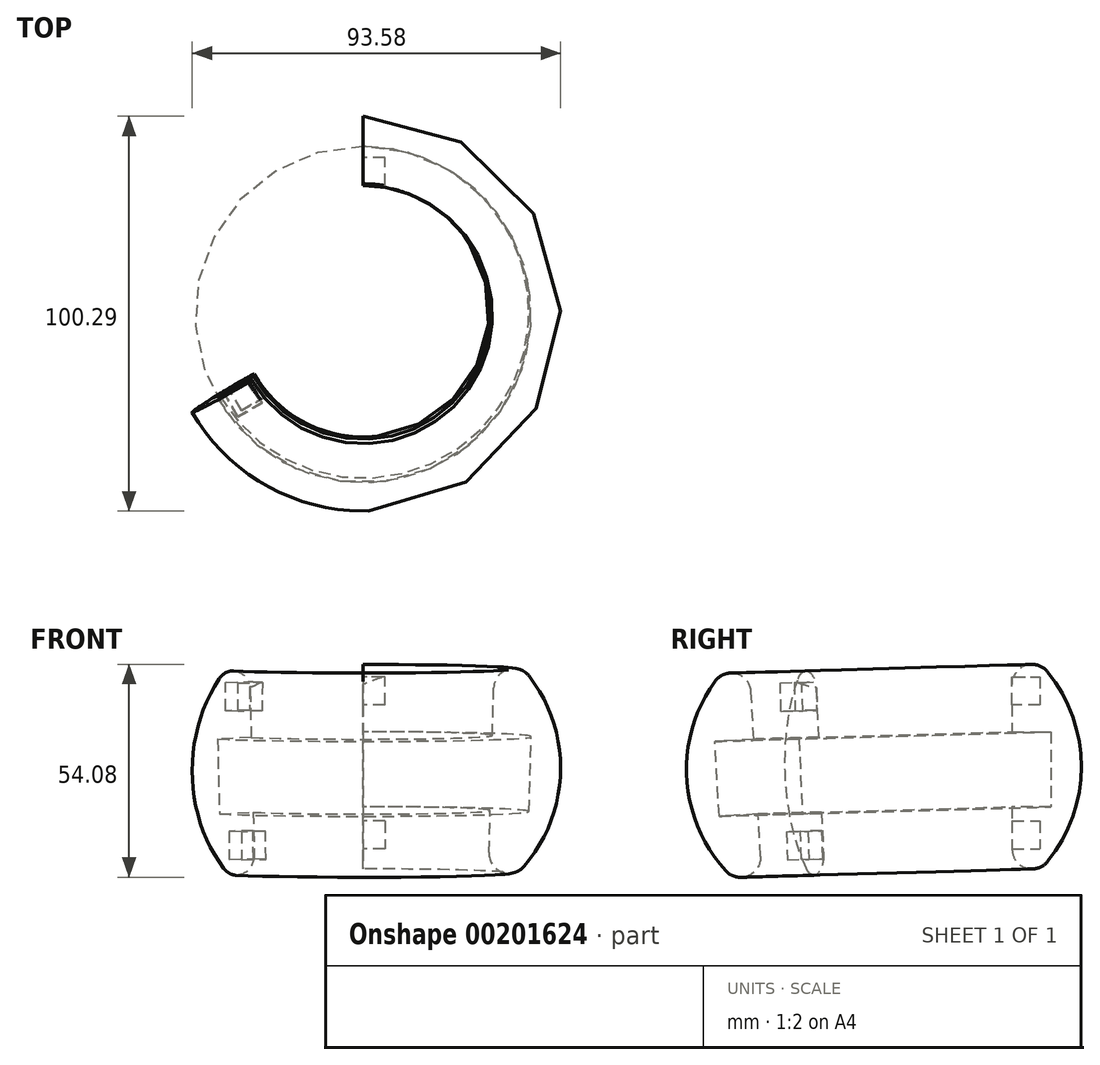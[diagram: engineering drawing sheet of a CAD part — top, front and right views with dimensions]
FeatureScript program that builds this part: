
annotation { "Feature Type Name" : "Feature", "Feature Type Description" : "" }
export const myFeature = defineFeature(function(context is Context, id is Id, definition is map)
    precondition{}
    {
        {
            var Q0;
            Q0=qCreatedBy(makeId("Right.planeOp"),FACE);
            var sketch = newSketch(context, id + "F0", { "sketchPlane" : qUnion([Q0])});
            skArc(sketch, "E0", {"start": v(0, -47.93) * mm, "mid": v(17.57, -15.75) * mm, "end": v(0, 16.43) * mm});
            skLineSegment(sketch, "E1", {"start": v(0, 16.43) * mm, "end": v(0, -6.89) * mm});
            skLineSegment(sketch, "E2", {"start": v(0, -6.89) * mm, "end": v(9.88, -6.89) * mm});
            skLineSegment(sketch, "E3", {"start": v(9.88, -6.89) * mm, "end": v(9.88, -25.94) * mm});
            skLineSegment(sketch, "E4", {"start": v(9.88, -25.94) * mm, "end": v(0, -25.94) * mm});
            skLineSegment(sketch, "E5", {"start": v(0, -25.94) * mm, "end": v(0, -47.93) * mm});
            skSolve(sketch);
        }
        {
            var Q0;
            Q0=qCreatedBy(makeId("Right.planeOp"),FACE);
            var sketch = newSketch(context, id + "F1", { "sketchPlane" : qUnion([Q0])});
            skPoint(sketch, "E6", {"position": v(-32.7, -11.9) * mm});
            skLineSegment(sketch, "E7", {"start": v(-33.24, 7.35) * mm, "end": v(-32.7, -11.9) * mm});
            skSolve(sketch);
        }
        {
            var Q0;
            Q0=qSketchRegion(id+"F0",true);
            var Q1;
            Q1=sQuery(id+"F1.wireOp",EDGE,"E7");
            revolve(context, id + "F2", {"entities" : qUnion([Q0]), "axis" : qUnion([Q1]), "revolveType" : RevolveType.ONE_DIRECTION, "angle" : 240 * degree});
        }
        {
            var Q0;
            Q0=qCreatedBy(makeId("Right.planeOp"),FACE);
            var sketch = newSketch(context, id + "F3", { "sketchPlane" : qUnion([Q0])});
            skLineSegment(sketch, "E8", {"start": v(0, 7.11) * mm, "end": v(7.11, 7.11) * mm});
            skLineSegment(sketch, "E9", {"start": v(7.11, 7.11) * mm, "end": v(7.11, 0) * mm});
            skLineSegment(sketch, "E10", {"start": v(7.11, 0) * mm, "end": v(0, 0) * mm});
            skLineSegment(sketch, "E11", {"start": v(0, 0) * mm, "end": v(0, 7.11) * mm});
            skSolve(sketch);
        }
        {
            var Q0;
            Q0=makeQuery(id+"F3.imprint","IMPRINT",FACE,{"disambiguationData":[TD([[makeQuery(id+"F3.imprint","IMPRINT",EDGE,{"derivedFrom":sQuery(id+"F3.wireOp",EDGE,"E8")}),-1.0]])]});
            extrude(context, id + "F4", {"entities" : qUnion([Q0]), "operationType" : NewBodyOperationType.REMOVE, "depth" : 5.56 * mm});
        }
        {
            var Q0;
            Q0=qCreatedBy(makeId("Right.planeOp"),FACE);
            var sketch = newSketch(context, id + "F5", { "sketchPlane" : qUnion([Q0])});
            skLineSegment(sketch, "E12", {"start": v(0, -29.58) * mm, "end": v(0, -36.7) * mm});
            skLineSegment(sketch, "E13", {"start": v(0, -36.7) * mm, "end": v(7.11, -36.7) * mm});
            skLineSegment(sketch, "E14", {"start": v(0, -29.58) * mm, "end": v(7.11, -29.58) * mm});
            skLineSegment(sketch, "E15", {"start": v(7.11, -29.58) * mm, "end": v(7.11, -36.7) * mm});
            skSolve(sketch);
        }
        {
            var Q0;
            Q0=qSketchRegion(id+"F5",true);
            extrude(context, id + "F6", {"entities" : qUnion([Q0]), "operationType" : NewBodyOperationType.REMOVE, "depth" : 5.56 * mm});
        }
        {
            var Q0;
            Q0=makeQuery(id+"F2.opRevolve","SWEPT_EDGE",EDGE,{"disambiguationData":[OSD([sQuery(id+"F0.wireOp",EDGE,"E0"),sQuery(id+"F0.wireOp",EDGE,"E5")])]});
            fillet(context, id + "F7", {"entities" : qUnion([Q0]), "radius" : 5.08 * mm, "tangentPropagation" : true, "allowEdgeOverflow" : false});
        }
        {
            var Q0;
            Q0=makeQuery(id+"F2.opRevolve","SWEPT_EDGE",EDGE,{"disambiguationData":[OSD([sQuery(id+"F0.wireOp",EDGE,"E0"),sQuery(id+"F0.wireOp",EDGE,"E1")])]});
            fillet(context, id + "F8", {"entities" : qUnion([Q0]), "radius" : 5.08 * mm, "tangentPropagation" : true, "allowEdgeOverflow" : false});
        }
        {
            var Q0;
            Q0=makeQuery(id+"F2.opRevolve","CAP_FACE",FACE,{"disambiguationData":[OSD([sQuery(id+"F0.wireOp",EDGE,"E0"),sQuery(id+"F0.wireOp",EDGE,"E1"),sQuery(id+"F0.wireOp",EDGE,"E2"),sQuery(id+"F0.wireOp",EDGE,"E3"),sQuery(id+"F0.wireOp",EDGE,"E4"),sQuery(id+"F0.wireOp",EDGE,"E5")])],"isStart":false});
            cPlane(context, id + "F9", {"entities" : qUnion([Q0]), "cplaneType" : CPlaneType.OFFSET, "offset" : 0 * mm, "oppositeDirection" : true, "width" : 152.4 * mm, "height" : 152.4 * mm});
        }
        {
            var Q0;
            Q0=qCreatedBy(id+"F9.planeOp",FACE);
            var sketch = newSketch(context, id + "F10", { "sketchPlane" : qUnion([Q0])});
            skLineSegment(sketch, "E16", {"start": v(49.81, 0) * mm, "end": v(56.9, 0) * mm});
            skLineSegment(sketch, "E17", {"start": v(56.9, 0) * mm, "end": v(56.9, 7.21) * mm});
            skLineSegment(sketch, "E18", {"start": v(56.9, 7.21) * mm, "end": v(49.75, 7.21) * mm});
            skLineSegment(sketch, "E19", {"start": v(49.75, 7.21) * mm, "end": v(49.81, 0) * mm});
            skSolve(sketch);
        }
        {
            var Q0;
            Q0=qSketchRegion(id+"F10",true);
            extrude(context, id + "F11", {"entities" : qUnion([Q0]), "operationType" : NewBodyOperationType.REMOVE, "oppositeDirection" : true, "depth" : 6.35 * mm});
        }
        {
            var Q0;
            Q0=qCreatedBy(id+"F9.planeOp",FACE);
            var sketch = newSketch(context, id + "F12", { "sketchPlane" : qUnion([Q0])});
            skLineSegment(sketch, "E20", {"start": v(48.78, -30.64) * mm, "end": v(55.9, -30.64) * mm});
            skLineSegment(sketch, "E21", {"start": v(55.9, -30.64) * mm, "end": v(55.9, -37.75) * mm});
            skLineSegment(sketch, "E22", {"start": v(55.9, -37.75) * mm, "end": v(48.72, -37.75) * mm});
            skLineSegment(sketch, "E23", {"start": v(48.72, -37.75) * mm, "end": v(48.78, -30.64) * mm});
            skSolve(sketch);
        }
        {
            var Q0;
            Q0=qSketchRegion(id+"F12",true);
            extrude(context, id + "F13", {"entities" : qUnion([Q0]), "operationType" : NewBodyOperationType.REMOVE, "oppositeDirection" : true, "depth" : 6.35 * mm});
        }
    });
